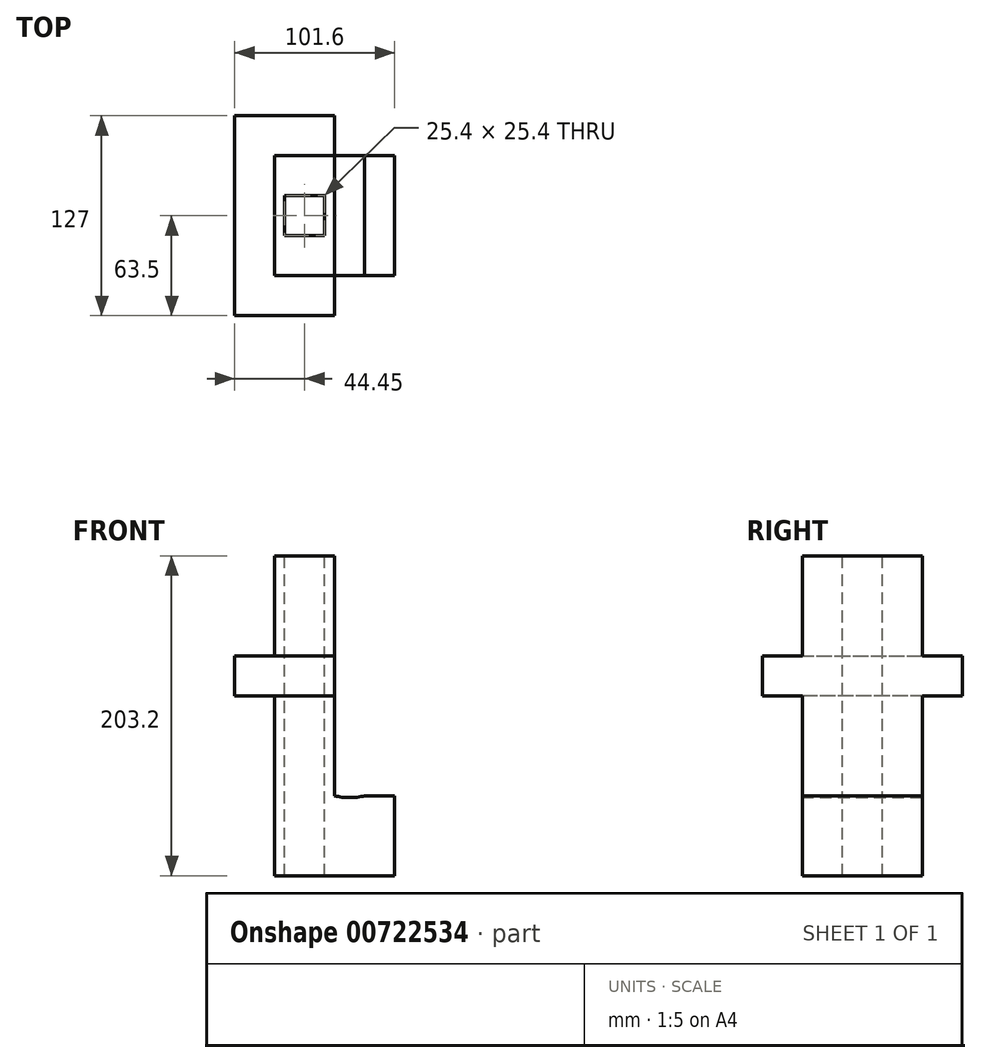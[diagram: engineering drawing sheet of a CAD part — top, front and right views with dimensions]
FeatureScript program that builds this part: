
annotation { "Feature Type Name" : "Feature", "Feature Type Description" : "" }
export const myFeature = defineFeature(function(context is Context, id is Id, definition is map)
    precondition{}
    {
        {
            var Q0;
            Q0=qCreatedBy(makeId("Top.planeOp"),FACE);
            var sketch = newSketch(context, id + "F0", { "sketchPlane" : qUnion([Q0])});
            skLineSegment(sketch, "E0.bottom", {"start": v(19.05, -38.1) * mm, "end": v(-19.05, -38.1) * mm});
            skLineSegment(sketch, "E0.top", {"start": v(19.05, 38.1) * mm, "end": v(-19.05, 38.1) * mm});
            skLineSegment(sketch, "E0.left", {"start": v(19.05, -38.1) * mm, "end": v(19.05, 38.1) * mm});
            skLineSegment(sketch, "E0.right", {"start": v(-19.05, -38.1) * mm, "end": v(-19.05, 38.1) * mm});
            skPoint(sketch, "E0.middle", {"position": v(0, 0) * mm});
            skSolve(sketch);
        }
        {
            var Q0;
            Q0=makeQuery(id+"F0.imprint","IMPRINT",FACE,{"disambiguationData":[TD([[makeQuery(id+"F0.imprint","IMPRINT",EDGE,{"derivedFrom":sQuery(id+"F0.wireOp",EDGE,"E0.bottom")}),-1.0]])]});
            extrude(context, id + "F1", {"entities" : qUnion([Q0]), "depth" : 177.8 * mm, "offsetDistance" : 25.4 * mm});
        }
        {
            var Q0;
            Q0=makeQuery(id+"F1.opExtrude","SWEPT_FACE",FACE,{"disambiguationData":[OSD([sQuery(id+"F0.wireOp",EDGE,"E0.right")])]});
            var sketch = newSketch(context, id + "F2", { "sketchPlane" : qUnion([Q0])});
            skLineSegment(sketch, "E1", {"start": v(38.1, 139.7) * mm, "end": v(-38.1, 139.7) * mm});
            skLineSegment(sketch, "E2", {"start": v(-38.1, 139.7) * mm, "end": v(-38.1, 114.3) * mm});
            skLineSegment(sketch, "E3", {"start": v(-38.1, 114.3) * mm, "end": v(38.1, 114.3) * mm});
            skLineSegment(sketch, "E4", {"start": v(38.1, 114.3) * mm, "end": v(38.1, 139.7) * mm});
            skSolve(sketch);
        }
        {
            var Q0;
            Q0=makeQuery(id+"F2.imprint","IMPRINT",FACE,{"disambiguationData":[TD([[makeQuery(id+"F2.imprint","IMPRINT",EDGE,{"derivedFrom":sQuery(id+"F2.wireOp",EDGE,"E1")}),1.0]])]});
            extrude(context, id + "F3", {"entities" : qUnion([Q0]), "operationType" : NewBodyOperationType.ADD, "depth" : 25.4 * mm, "offsetDistance" : 25.4 * mm});
        }
        {
            var Q0;
            Q0=makeQuery(id+"F3.boolean.opBoolean","MERGE",FACE,{"derivedFrom":[makeQuery(id+"F1.opExtrude","SWEPT_FACE",FACE,{"disambiguationData":[OSD([sQuery(id+"F0.wireOp",EDGE,"E0.bottom")])]}),makeQuery(id+"F3.opExtrude","SWEPT_FACE",FACE,{"disambiguationData":[OSD([sQuery(id+"F2.wireOp",EDGE,"E4")])]})]});
            var sketch = newSketch(context, id + "F4", { "sketchPlane" : qUnion([Q0])});
            skLineSegment(sketch, "E5", {"start": v(-63.5, 114.3) * mm, "end": v(19.05, 114.3) * mm});
            skLineSegment(sketch, "E6", {"start": v(19.05, 114.3) * mm, "end": v(19.05, 139.7) * mm});
            skLineSegment(sketch, "E7", {"start": v(19.05, 139.7) * mm, "end": v(-44.45, 139.7) * mm});
            skSolve(sketch);
        }
        {
            var Q0;
            {var subQ11=sQuery(id+"F4.wireOp",EDGE,"E6");Q0=makeQuery(id+"F4.imprint","IMPRINT",FACE,{"disambiguationData":[TD([[makeQuery(id+"F4.imprint","IMPRINT",EDGE,{"derivedFrom":subQ11}),-1.0]])]});}
            extrude(context, id + "F5", {"entities" : qUnion([Q0]), "operationType" : NewBodyOperationType.ADD, "depth" : 25.4 * mm, "offsetDistance" : 25.4 * mm});
        }
        {
            var Q0;
            Q0=makeQuery(id+"F3.boolean.opBoolean","MERGE",FACE,{"derivedFrom":[makeQuery(id+"F1.opExtrude","SWEPT_FACE",FACE,{"disambiguationData":[OSD([sQuery(id+"F0.wireOp",EDGE,"E0.top")])]}),makeQuery(id+"F3.opExtrude","SWEPT_FACE",FACE,{"disambiguationData":[OSD([sQuery(id+"F2.wireOp",EDGE,"E2")])]})]});
            var sketch = newSketch(context, id + "F6", { "sketchPlane" : qUnion([Q0])});
            skLineSegment(sketch, "E8", {"start": v(44.45, 139.7) * mm, "end": v(-19.05, 139.7) * mm});
            skLineSegment(sketch, "E9", {"start": v(-19.05, 139.7) * mm, "end": v(-19.05, 114.3) * mm});
            skLineSegment(sketch, "E10", {"start": v(-19.05, 114.3) * mm, "end": v(44.45, 114.3) * mm});
            skSolve(sketch);
        }
        {
            var Q0;
            Q0=qSketchRegion(id+"F6",true);
            var Q1;
            {var subQ11=sQuery(id+"F6.wireOp",EDGE,"E9");Q1=makeQuery(id+"F6.imprint","IMPRINT",FACE,{"disambiguationData":[TD([[makeQuery(id+"F6.imprint","IMPRINT",EDGE,{"derivedFrom":subQ11}),1.0]])]});}
            extrude(context, id + "F7", {"entities" : qUnion([Q0, Q1]), "operationType" : NewBodyOperationType.ADD, "depth" : 25.4 * mm, "offsetDistance" : 25.4 * mm});
        }
        {
            var Q0;
            Q0=makeQuery(id+"F1.opExtrude","CAP_FACE",FACE,{"disambiguationData":[OSD([sQuery(id+"F0.wireOp",EDGE,"E0.bottom"),sQuery(id+"F0.wireOp",EDGE,"E0.top"),sQuery(id+"F0.wireOp",EDGE,"E0.left"),sQuery(id+"F0.wireOp",EDGE,"E0.right")])],"isStart":false});
            var sketch = newSketch(context, id + "F8", { "sketchPlane" : qUnion([Q0])});
            skLineSegment(sketch, "E11.bottom", {"start": v(-19.05, 38.1) * mm, "end": v(19.05, 38.1) * mm});
            skLineSegment(sketch, "E11.top", {"start": v(-19.05, -38.1) * mm, "end": v(19.05, -38.1) * mm});
            skLineSegment(sketch, "E11.left", {"start": v(-19.05, 38.1) * mm, "end": v(-19.05, -38.1) * mm});
            skLineSegment(sketch, "E11.right", {"start": v(19.05, 38.1) * mm, "end": v(19.05, -38.1) * mm});
            skSolve(sketch);
        }
        {
            var Q0;
            Q0=makeQuery(id+"F8.imprint","IMPRINT",FACE,{"disambiguationData":[TD([[makeQuery(id+"F8.imprint","IMPRINT",EDGE,{"derivedFrom":sQuery(id+"F8.wireOp",EDGE,"E11.bottom")}),1.0]])]});
            extrude(context, id + "F9", {"entities" : qUnion([Q0]), "operationType" : NewBodyOperationType.ADD, "depth" : 25.4 * mm, "offsetDistance" : 25.4 * mm});
        }
        {
            var Q0;
            Q0=makeQuery(id+"F9.opExtrude","CAP_FACE",FACE,{"disambiguationData":[OSD([sQuery(id+"F8.wireOp",EDGE,"E11.bottom"),sQuery(id+"F8.wireOp",EDGE,"E11.top"),sQuery(id+"F8.wireOp",EDGE,"E11.left"),sQuery(id+"F8.wireOp",EDGE,"E11.right")])],"isStart":false});
            var sketch = newSketch(context, id + "F10", { "sketchPlane" : qUnion([Q0])});
            skLineSegment(sketch, "E12", {"start": v(-12.7, 12.7) * mm, "end": v(-12.7, -12.7) * mm});
            skLineSegment(sketch, "E13", {"start": v(-12.7, -12.7) * mm, "end": v(12.7, -12.7) * mm});
            skLineSegment(sketch, "E14", {"start": v(12.7, -12.7) * mm, "end": v(12.7, 12.7) * mm});
            skLineSegment(sketch, "E15", {"start": v(12.7, 12.7) * mm, "end": v(-12.7, 12.7) * mm});
            skSolve(sketch);
        }
        {
            var Q0;
            Q0=qSketchRegion(id+"F10",true);
            extrude(context, id + "F11", {"entities" : qUnion([Q0]), "operationType" : NewBodyOperationType.REMOVE, "oppositeDirection" : true, "depth" : 228.6 * mm, "offsetDistance" : 25.4 * mm});
        }
        {
            var Q0;
            Q0=makeQuery(id+"F9.boolean.opBoolean","MERGE",FACE,{"derivedFrom":[makeQuery(id+"F7.boolean.opBoolean","MERGE",FACE,{"derivedFrom":[makeQuery(id+"F5.boolean.opBoolean","MERGE",FACE,{"derivedFrom":[makeQuery(id+"F1.opExtrude","SWEPT_FACE",FACE,{"disambiguationData":[OSD([sQuery(id+"F0.wireOp",EDGE,"E0.left")])]}),makeQuery(id+"F5.opExtrude","SWEPT_FACE",FACE,{"disambiguationData":[OSD([sQuery(id+"F4.wireOp",EDGE,"E6")])]})]}),makeQuery(id+"F7.opExtrude","SWEPT_FACE",FACE,{"disambiguationData":[OSD([sQuery(id+"F6.wireOp",EDGE,"E9")])]})]}),makeQuery(id+"F9.opExtrude","SWEPT_FACE",FACE,{"disambiguationData":[OSD([sQuery(id+"F8.wireOp",EDGE,"E11.right")])]})]});
            var sketch = newSketch(context, id + "F12", { "sketchPlane" : qUnion([Q0])});
            skLineSegment(sketch, "E16", {"start": v(-38.1, 0) * mm, "end": v(-38.1, 50.8) * mm});
            skLineSegment(sketch, "E17", {"start": v(-38.1, 50.8) * mm, "end": v(38.1, 50.8) * mm});
            skLineSegment(sketch, "E18", {"start": v(38.1, 50.8) * mm, "end": v(38.1, 0) * mm});
            skLineSegment(sketch, "E19", {"start": v(38.1, 0) * mm, "end": v(-38.1, 0) * mm});
            skSolve(sketch);
        }
        {
            var Q0;
            Q0=makeQuery(id+"F12.imprint","IMPRINT",FACE,{"disambiguationData":[TD([[makeQuery(id+"F12.imprint","IMPRINT",EDGE,{"derivedFrom":sQuery(id+"F12.wireOp",EDGE,"E16")}),1.0]])]});
            extrude(context, id + "F13", {"entities" : qUnion([Q0]), "operationType" : NewBodyOperationType.ADD, "depth" : 38.1 * mm, "offsetDistance" : 25.4 * mm});
        }
        {
            var Q0;
            {var subQ2=sQuery(id+"F0.wireOp",EDGE,"E0.bottom");Q0=makeQuery(id+"F13.boolean.opBoolean","MERGE",FACE,{"derivedFrom":[makeQuery(id+"F5.boolean.opBoolean","SPLIT",FACE,{"disambiguationData":[TD([makeQuery(id+"F3.opExtrude","SWEPT_FACE",FACE,{"disambiguationData":[OSD([sQuery(id+"F2.wireOp",EDGE,"E3")])]})])],"derivedFrom":makeQuery(id+"F3.boolean.opBoolean","MERGE",FACE,{"derivedFrom":[makeQuery(id+"F1.opExtrude","SWEPT_FACE",FACE,{"disambiguationData":[OSD([subQ2])]}),makeQuery(id+"F3.opExtrude","SWEPT_FACE",FACE,{"disambiguationData":[OSD([sQuery(id+"F2.wireOp",EDGE,"E4")])]})]})}),makeQuery(id+"F13.opExtrude","SWEPT_FACE",FACE,{"disambiguationData":[OSD([sQuery(id+"F12.wireOp",EDGE,"E16")])]})]});}
            var sketch = newSketch(context, id + "F14", { "sketchPlane" : qUnion([Q0])});
            skArc(sketch, "E20", {"start": v(19.05, 50.8) * mm, "mid": v(28.58, 49.6) * mm, "end": v(38.1, 50.8) * mm});
            skSolve(sketch);
        }
        {
            var Q0;
            {var subQ0=sQuery(id+"F14.wireOp",EDGE,"E20");Q0=makeQuery(id+"F14.imprint","IMPRINT",FACE,{"disambiguationData":[TD([[makeQuery(id+"F14.imprint","IMPRINT",EDGE,{"derivedFrom":subQ0}),1.0]])]});}
            extrude(context, id + "F15", {"entities" : qUnion([Q0]), "operationType" : NewBodyOperationType.REMOVE, "oppositeDirection" : true, "depth" : 228.6 * mm, "offsetDistance" : 25.4 * mm});
        }
    });
